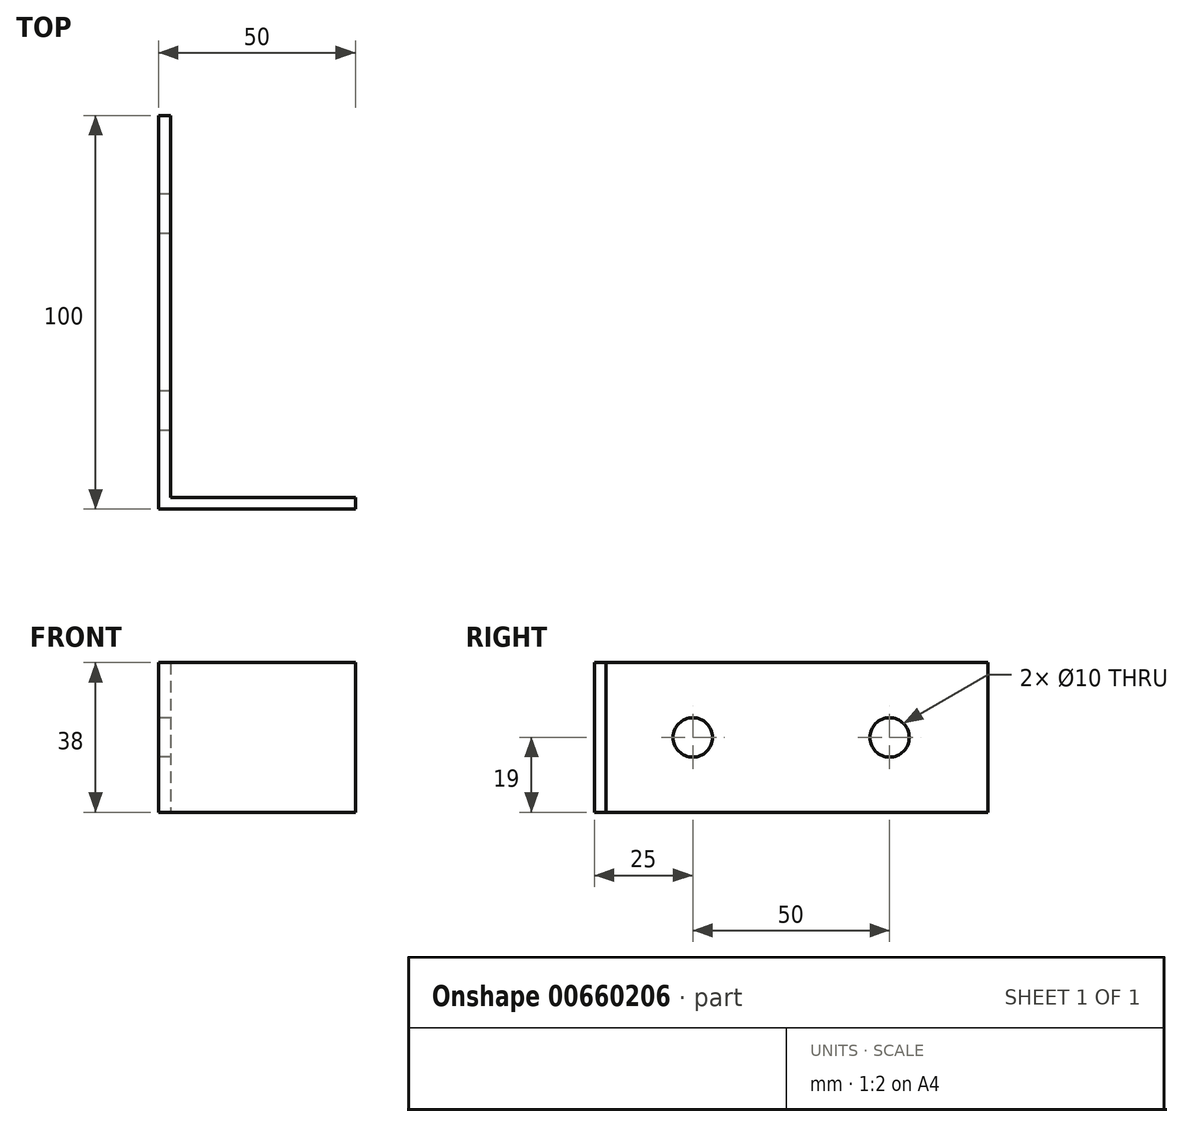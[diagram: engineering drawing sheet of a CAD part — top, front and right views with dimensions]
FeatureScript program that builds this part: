
annotation { "Feature Type Name" : "Feature", "Feature Type Description" : "" }
export const myFeature = defineFeature(function(context is Context, id is Id, definition is map)
    precondition{}
    {
        {
            var Q0;
            Q0=qCreatedBy(makeId("Top.planeOp"),FACE);
            var sketch = newSketch(context, id + "F0", { "sketchPlane" : qUnion([Q0])});
            skLineSegment(sketch, "E0.bottom", {"start": v(0, 0) * mm, "end": v(50, 0) * mm});
            skLineSegment(sketch, "E0.top", {"start": v(3, 3) * mm, "end": v(50, 3) * mm});
            skLineSegment(sketch, "E0.left", {"start": v(0, 0) * mm, "end": v(0, 3) * mm});
            skLineSegment(sketch, "E0.right", {"start": v(50, 0) * mm, "end": v(50, 3) * mm});
            skLineSegment(sketch, "E1.bottom", {"start": v(0, 0) * mm, "end": v(3, 0) * mm});
            skLineSegment(sketch, "E1.top", {"start": v(0, 100) * mm, "end": v(3, 100) * mm});
            skLineSegment(sketch, "E1.left", {"start": v(0, 0) * mm, "end": v(0, 100) * mm});
            skLineSegment(sketch, "E1.right", {"start": v(3, 3) * mm, "end": v(3, 100) * mm});
            skSolve(sketch);
        }
        {
            var Q0;
            Q0 = qSketchRegion(id + "F0", true);
            extrude(context, id + "F1", {"entities" : qUnion([Q0]), "depth" : 38 * mm, "offsetDistance" : 25 * mm});
        }
        {
            var Q0;
            Q0=makeQuery(id+"F1.opExtrude","SWEPT_FACE",FACE,{"disambiguationData":[OSD([sQuery(id+"F0.wireOp",EDGE,"E1.left")])]});
            var sketch = newSketch(context, id + "F2", { "sketchPlane" : qUnion([Q0])});
            skCircle(sketch, "E2", {"center": v(-75, 19) * mm, "radius": 5 * mm});
            skCircle(sketch, "E3", {"center": v(-25, 19) * mm, "radius": 5 * mm});
            skSolve(sketch);
        }
        {
            var Q0;
            Q0 = qSketchRegion(id + "F2", true);
            extrude(context, id + "F3", {"entities" : qUnion([Q0]), "operationType" : NewBodyOperationType.REMOVE, "oppositeDirection" : true, "depth" : 25 * mm, "offsetDistance" : 25 * mm});
        }
    });
